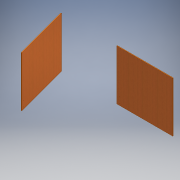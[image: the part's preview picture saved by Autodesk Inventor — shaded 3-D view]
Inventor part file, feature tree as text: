
AUTODESK INVENTOR PART (.ipt)
format: ipt  version: 2016 (Build 200138000, 138)  size: 175,616 bytes
history: native  units: mm
features: extrude x4, sketch x4, projected_geometry x2, plane x1
ambient origin geometry x8: Origin, YZ Plane, XZ Plane, XY Plane, X Axis, Y Axis, Z Axis, Center Point
bodies: Solid1 (feature_tree)
feature tree (11):
  plane  "Plano de trabajo4"
  extrude  "Extrusión8"  Depth=1180.0mm
  extrude  "Extrusión9"  TaperAngle=0.0deg  [1 undecoded]
  extrude  "Extrusión10"  Depth=80.0mm
  extrude  "Extrusión11"  Depth=730.0mm
  sketch  "Boceto8"  dims[d38=290.0mm d39=1180.0mm]
  sketch  "Boceto9"  dims[d40=10.0mm d42=0.0mm]
  projected_geometry  "Contorno proyectado7"
  sketch  "Boceto10"  dims[d43=59.0mm d44=80.0mm]
  sketch  "Boceto11"  dims[d45=6.0mm d46=50.0mm d47=740.0mm d48=0.0mm d49=1180.0mm d50=1180.0mm d52=10.0mm d53=1180.0mm d54=730.0mm d55=0.0mm d56=59.0mm d57=80.0mm d58=6.0mm d59=50.0mm d60=730.0mm d61=0.0mm]
  projected_geometry  "Contorno proyectado8"
note: 1 required parameter value undecoded (feature->parameter linkage not recoverable at this tier; creation-order binding heuristic only, values carry confidence <= 0.55)
